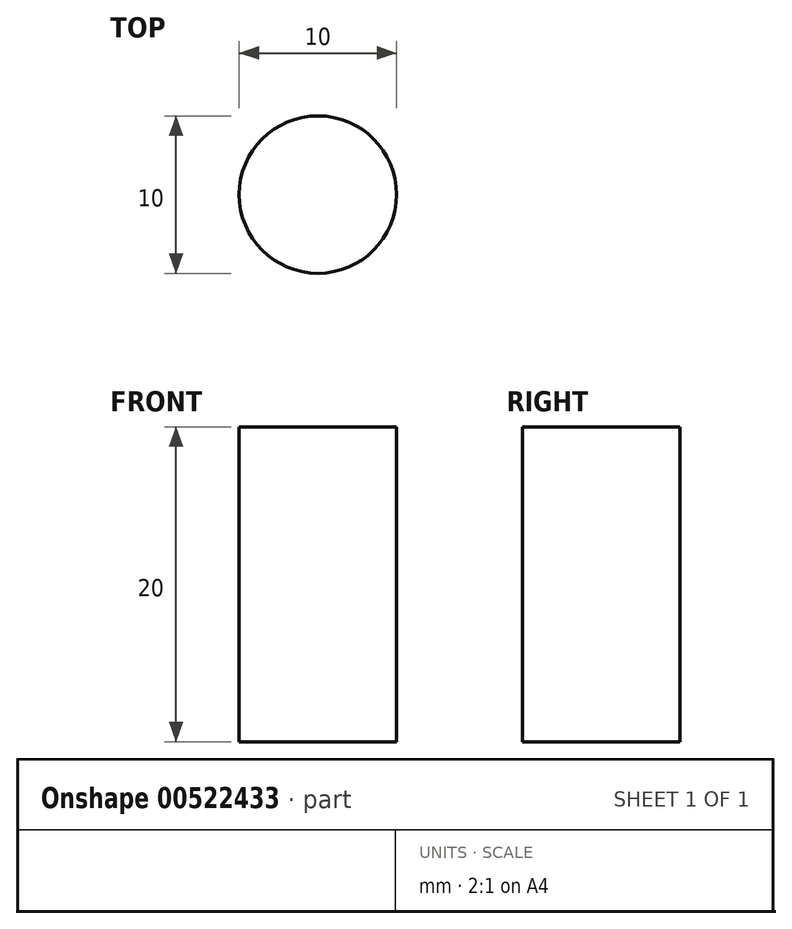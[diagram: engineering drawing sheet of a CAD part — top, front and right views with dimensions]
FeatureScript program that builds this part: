
annotation { "Feature Type Name" : "Feature", "Feature Type Description" : "" }
export const myFeature = defineFeature(function(context is Context, id is Id, definition is map)
    precondition{}
    {
        {
            var Q0;
            Q0=qCreatedBy(makeId("Top.planeOp"),FACE);
            var sketch = newSketch(context, id + "F0", { "sketchPlane" : qUnion([Q0])});
            skCircle(sketch, "E0", {"center": v(0, 0) * mm, "radius": 5 * mm});
            skSolve(sketch);
        }
        {
            var Q0;
            Q0=makeQuery(id+"F0.imprint","IMPRINT",FACE,{"disambiguationData":[TD([[makeQuery(id+"F0.imprint","IMPRINT",EDGE,{"derivedFrom":sQuery(id+"F0.wireOp",EDGE,"E0")}),1.0]])]});
            extrude(context, id + "F1", {"entities" : qUnion([Q0]), "depth" : 20 * mm, "offsetDistance" : 25 * mm});
        }
    });
